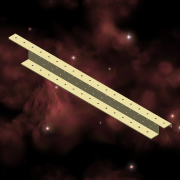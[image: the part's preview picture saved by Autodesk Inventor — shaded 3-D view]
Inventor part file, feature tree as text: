
AUTODESK INVENTOR PART (.ipt)
format: ipt  version: 2015 SP1 (Build 190203100, 203)  size: 571,392 bytes
history: native  units: in
note: dims shown in document units (in); Inventor stores cm internally (conversion verified against a paired STEP export)
features: plane x4, other x2, extrude x2, sketch x2, fillet x1, imported_body x1
ambient origin geometry x8: Origin, YZ Plane, XZ Plane, XY Plane, X Axis, Y Axis, Z Axis, Center Point
bodies: Body1 (feature_tree)
feature tree (12):
  other  "Break-Corner1"
  other  "1 x 2 x 1 x 0.090 C-Channel (59 length)1"
  plane  "Work Plane1"
  extrude  "Extrusion1"  Depth=1.0in TaperAngle=0.0deg
  plane  "Work Plane2"
  plane  "Work Plane3"
  plane  "Work Plane4"
  extrude  "Extrusion5"  Depth=0.25in
  fillet  "Fillet1"  Radius=1.0in
  imported_body  "Base1"
  sketch  "Sketch1"  dims[d0=19.0in d1=1.0in d2=0.0in]
  sketch  "Sketch5"  dims[d7=0.1875in d12=9.5in d13=1.0in d14=0.0in d15=0.25in]
